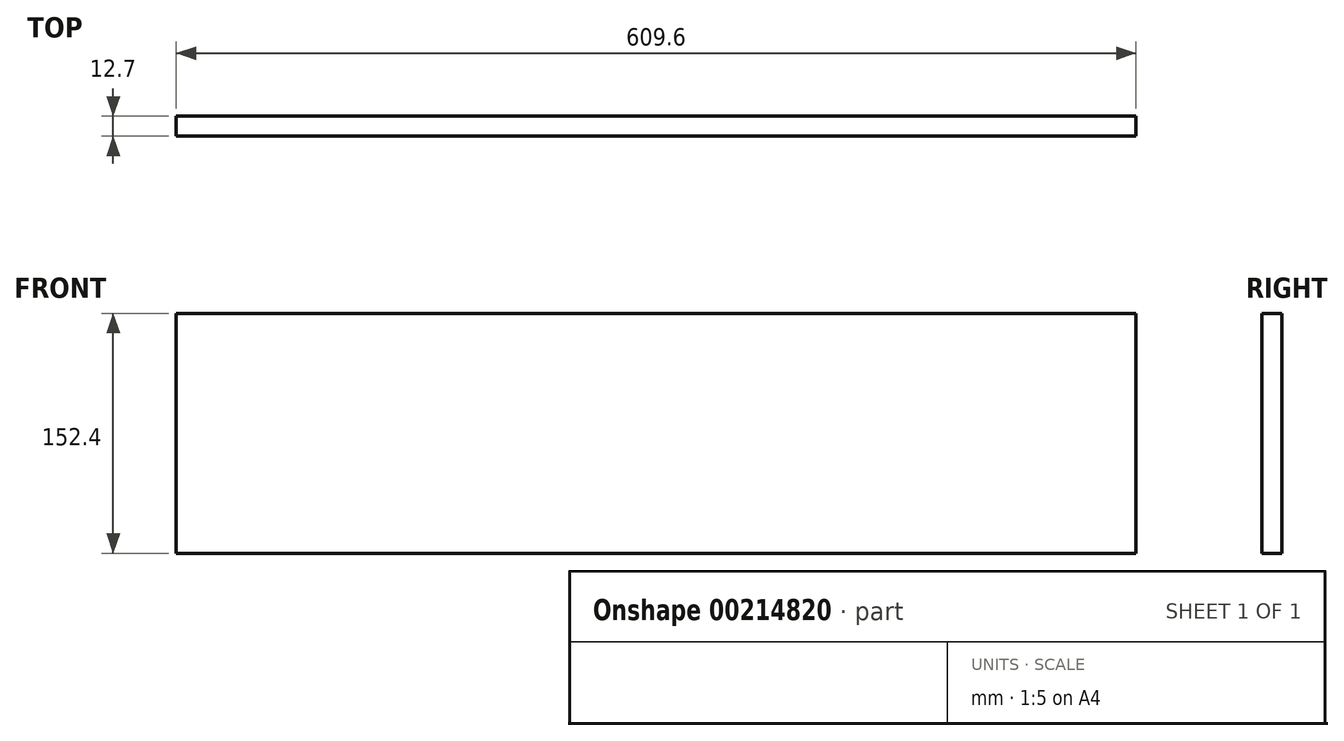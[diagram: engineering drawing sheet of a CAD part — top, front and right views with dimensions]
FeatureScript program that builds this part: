
annotation { "Feature Type Name" : "Feature", "Feature Type Description" : "" }
export const myFeature = defineFeature(function(context is Context, id is Id, definition is map)
    precondition{}
    {
        {
            var Q0;
            Q0=qCreatedBy(makeId("Front.planeOp"),FACE);
            var sketch = newSketch(context, id + "F0", { "sketchPlane" : qUnion([Q0])});
            skLineSegment(sketch, "E0.bottom", {"start": v(0, 0) * mm, "end": v(609.6, 0) * mm});
            skLineSegment(sketch, "E0.top", {"start": v(0, -152.4) * mm, "end": v(609.6, -152.4) * mm});
            skLineSegment(sketch, "E0.left", {"start": v(0, 0) * mm, "end": v(0, -152.4) * mm});
            skLineSegment(sketch, "E0.right", {"start": v(609.6, 0) * mm, "end": v(609.6, -152.4) * mm});
            skSolve(sketch);
        }
        {
            var Q0;
            Q0=makeQuery(id+"F0.imprint","IMPRINT",FACE,{"disambiguationData":[TD([[makeQuery(id+"F0.imprint","IMPRINT",EDGE,{"derivedFrom":sQuery(id+"F0.wireOp",EDGE,"E0.bottom")}),-1.0]])]});
            extrude(context, id + "F1", {"entities" : qUnion([Q0]), "depth" : 12.7 * mm});
        }
    });
